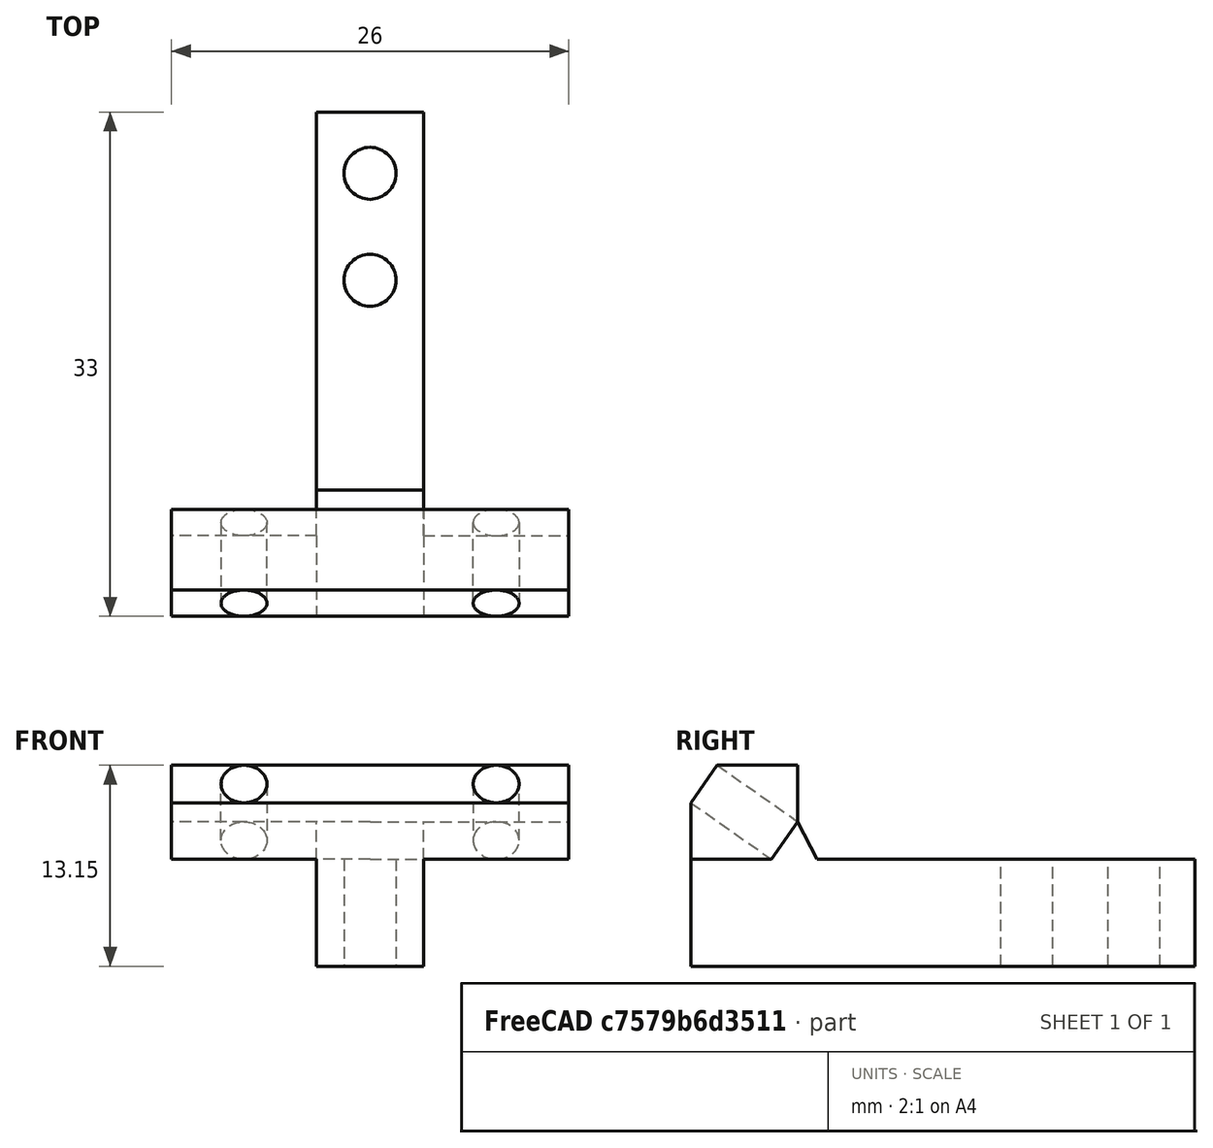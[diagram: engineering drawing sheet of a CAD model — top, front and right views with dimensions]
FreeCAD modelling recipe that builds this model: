
FCSTD DOCUMENT  (FreeCAD 0.19R24291 (Git))
Label: Иголки 55 1
License: All rights reserved
LicenseURL: http://en.wikipedia.org/wiki/All_rights_reserved
objects: Sketcher::SketchObject×5, Mesh::Feature×2, PartDesign::Pad×2, PartDesign::Pocket×1, PartDesign::Chamfer×1, PartDesign::Mirrored×1, PartDesign::Body×1
note: 15 computed .brp shape members not serialized (recipe doc carries the construction recipe); baked Part::Feature solids carry a one-line shape summary decoded from their .brp

FEATURE [Mesh::Feature] _5Angle  label="45Angle"
FEATURE [Sketcher::SketchObject] Sketch
  FullyConstrained = true
  MapMode = 5
  Support = -> [XY_Plane]
  sketch-geometry (8):
    g0: ArcOfCircle CenterX=0 CenterY=22 CenterZ=0 NormalX=0 NormalY=0 NormalZ=1 AngleXU=0 Radius=1.7 StartAngle=1.5708 EndAngle=4.71239
    g1: ArcOfCircle CenterX=0 CenterY=29 CenterZ=0 NormalX=0 NormalY=0 NormalZ=1 AngleXU=0 Radius=1.7 StartAngle=1.5708 EndAngle=4.71239
    g2: LineSegment StartX=1e-16 StartY=30.7 StartZ=0 EndX=0 EndY=33 EndZ=0
    g3: LineSegment StartX=0 StartY=33 StartZ=0 EndX=-3.5 EndY=33 EndZ=0
    g4: LineSegment StartX=-3.5 StartY=33 StartZ=0 EndX=-3.5 EndY=0 EndZ=0
    g5: LineSegment StartX=-3.5 StartY=0 StartZ=0 EndX=0 EndY=0 EndZ=0
    g6: LineSegment StartX=0 StartY=0 StartZ=0 EndX=0 EndY=20.3 EndZ=0
    g7: LineSegment StartX=-3e-16 StartY=27.3 StartZ=0 EndX=1e-16 EndY=23.7 EndZ=0
  constraints (26):
    c: PointOnObject(g0,g-2)
    c: PointOnObject(g0,g-2)
    c: PointOnObject(g0,g-2)
    c: PointOnObject(g1,g-2)
    c: PointOnObject(g1,g-2)
    c: PointOnObject(g1,g-2)
    c: Distance(g0,g1) = 7
    c: Distance(g0,g-1) = 22
    c: Equal(g0,g1)
    c: Diameter(g0) = 3.4
    c: Coincident(g2,g1)
    c: PointOnObject(g2,g-2)
    c: Coincident(g2,g3)
    c: Horizontal(g3)
    c: Coincident(g3,g4)
    c: PointOnObject(g4,g-1)
    c: Vertical(g4)
    c: Coincident(g4,g5)
    c: Coincident(g5,g-1)
    c: Coincident(g5,g6)
    c: Coincident(g6,g0)
    c: Distance(g2) = 2.3
    c: Distance(g3) = 3.5
    c: Coincident(g7,g1)
    c: Coincident(g7,g0)
    c: Distance(g4) = 33
FEATURE [PartDesign::Pad] Pad
  Direction = (1,1,1)
  Length = 7
  Length2 = 100
  Profile = -> Sketch
  Type = 0
FEATURE [Sketcher::SketchObject] Sketch003
  FullyConstrained = true
  MapMode = 5
  Placement = pos=(-3.5,0,0) rot=(0.57735,-0.57735,-0.57735;2.0944rad)
  Support = -> [Pad]
  sketch-geometry (4):
    g0: LineSegment StartX=0 StartY=0 StartZ=0 EndX=7.07107 EndY=7.07107 EndZ=0
    g1: LineSegment StartX=7.07107 StartY=7.07107 StartZ=0 EndX=0.707107 EndY=13.435 EndZ=0
    g2: LineSegment StartX=0.707107 StartY=13.435 StartZ=0 EndX=-6.36396 EndY=6.36396 EndZ=0
    g3: LineSegment StartX=-6.36396 StartY=6.36396 StartZ=0 EndX=0 EndY=0 EndZ=0
  constraints (11):
    c: Coincident(g-1,g0)
    c: Coincident(g0,g1)
    c: Coincident(g1,g2)
    c: Coincident(g2,g3)
    c: Coincident(g3,g0)
    c: Perpendicular(g1,g0)
    c: Perpendicular(g3,g0)
    c: Perpendicular(g2,g3)
    c: Angle(g-1,g0) = 0.785398
    c: Distance(g0) = 10
    c: Distance(g3) = 9
FEATURE [Sketcher::SketchObject] Sketch004
  FullyConstrained = false
  MapMode = 5
  Placement = pos=(0,6.36396,6.36396) rot=(0,0.382683,0.92388;3.14159rad)
  sketch-geometry (3):
    g0: Circle CenterX=7.5 CenterY=5 CenterZ=0 NormalX=0 NormalY=0 NormalZ=1 AngleXU=0 Radius=1
    g1: LineSegment StartX=0 StartY=10 StartZ=0 EndX=7.5 EndY=5 EndZ=0
    g2: LineSegment StartX=7.5 StartY=5 StartZ=0 EndX=0 EndY=0 EndZ=0
  constraints (6):
    c: Coincident(g1,g0)
    c: Coincident(g2,g0)
    c: Coincident(g2,g-1)
    c: Equal(g2,g1)
    c: Distance(g0,g-2) = 7.5
    c: Diameter(g0) = 2
FEATURE [Sketcher::SketchObject] Sketch005
  FullyConstrained = true
  MapMode = 5
  Placement = pos=(-3.5,0,0) rot=(0.57735,-0.57735,-0.57735;2.0944rad)
  Support = -> [Pad]
  sketch-geometry (8):
    g0: LineSegment StartX=0 StartY=7 StartZ=0 EndX=-5.27927 EndY=7 EndZ=0
    g1: LineSegment StartX=-7 StartY=9.45746 StartZ=0 EndX=-7 EndY=13.154 EndZ=0
    g2: LineSegment StartX=-7 StartY=13.154 StartZ=0 EndX=-1.72073 EndY=13.154 EndZ=0
    g3: LineSegment StartX=0 StartY=10.6966 StartZ=0 EndX=0 EndY=7 EndZ=0
    g4: LineSegment StartX=-1.72073 StartY=13.154 StartZ=0 EndX=0 EndY=10.6966 EndZ=0
    g5: LineSegment StartX=-7 StartY=9.45746 StartZ=0 EndX=-5.27927 EndY=7 EndZ=0
    g6: LineSegment StartX=-7 StartY=9.45746 StartZ=0 EndX=-1.72073 EndY=13.154 EndZ=0
    g7: LineSegment StartX=0 StartY=10.6966 StartZ=0 EndX=-5.27927 EndY=7 EndZ=0
  constraints (22):
    c: Coincident(g1,g2)
    c: Horizontal(g0)
    c: Horizontal(g2)
    c: Vertical(g1)
    c: Coincident(g6,g5)
    c: Coincident(g6,g4)
    c: Coincident(g7,g4)
    c: Coincident(g7,g5)
    c: Distance(g4) = 3
    c: Coincident(g2,g4)
    c: Coincident(g3,g4)
    c: Coincident(g0,g5)
    c: Coincident(g1,g5)
    c: Distance(g1,g-2) = 7
    c: PointOnObject(g3,g-2)
    c: Coincident(g0,g3)
    c: PointOnObject(g0,g-2)
    c: Distance(g0,g-1) = 7
    c: Angle(g7,g3) = 0.959931
    c: Perpendicular(g7,g4)
    c: Perpendicular(g5,g6)
    c: Perpendicular(g7,g5)
FEATURE [PartDesign::Pad] Pad001
  BaseFeature = -> Pad
  Direction = (1,1,1)
  Length = 9.5
  Length2 = 3.5
  Profile = -> Sketch005
  Type = 4
FEATURE [Sketcher::SketchObject] Sketch006
  ExternalGeometry = -> [Pad001]
  FullyConstrained = true
  MapMode = 5
  Placement = pos=(0,0.25352,-0.177516) rot=(0,0.887011,0.461749;3.14159rad)
  Support = -> [Pad001]
  sketch-geometry (3):
    g0: LineSegment StartX=13 StartY=11.7621 StartZ=0 EndX=3.5 EndY=8.76213 EndZ=0
    g1: LineSegment StartX=3.5 StartY=11.7621 StartZ=0 EndX=13 EndY=8.76213 EndZ=0
    g2: Circle CenterX=8.25 CenterY=10.2621 CenterZ=0 NormalX=0 NormalY=0 NormalZ=1 AngleXU=0 Radius=1.5
  constraints (8):
    c: PointOnObject(g2,g0)
    c: PointOnObject(g2,g1)
    c: Diameter(g2) = 3
    c: Coincident(g0,g-4)
    c: Coincident(g0,g-3)
    c: Coincident(g1,g-3)
    c: PointOnObject(g1,g-4)
    c: Vertical(g1,g0)
FEATURE [PartDesign::Pocket] Pocket
  BaseFeature = -> Pad001
  Length = 5
  Length2 = 100
  Profile = -> Sketch006
  Type = 1
FEATURE [PartDesign::Chamfer] Chamfer
  Angle = 45
  Base = -> Pocket [Edge18]
  BaseFeature = -> Pocket
  ChamferType = 0
  FlipDirection = false
  Size = 2.99
  Size2 = 1
  SupportTransform = false
FEATURE [PartDesign::Mirrored] Mirrored
  BaseFeature = -> Chamfer
  MirrorPlane = -> Sketch [V_Axis]
  Originals = -> [Pad,Pad001,Pocket,Chamfer]
FEATURE [PartDesign::Body] Body
  Group = -> [Sketch,Pad,Sketch003,Sketch004,Sketch005,Pad001,Sketch006,Pocket,Chamfer,Mirrored]
  Origin = -> Origin
  Tip = -> Mirrored
FEATURE [Mesh::Feature] ____________2  label="Иголки2"
